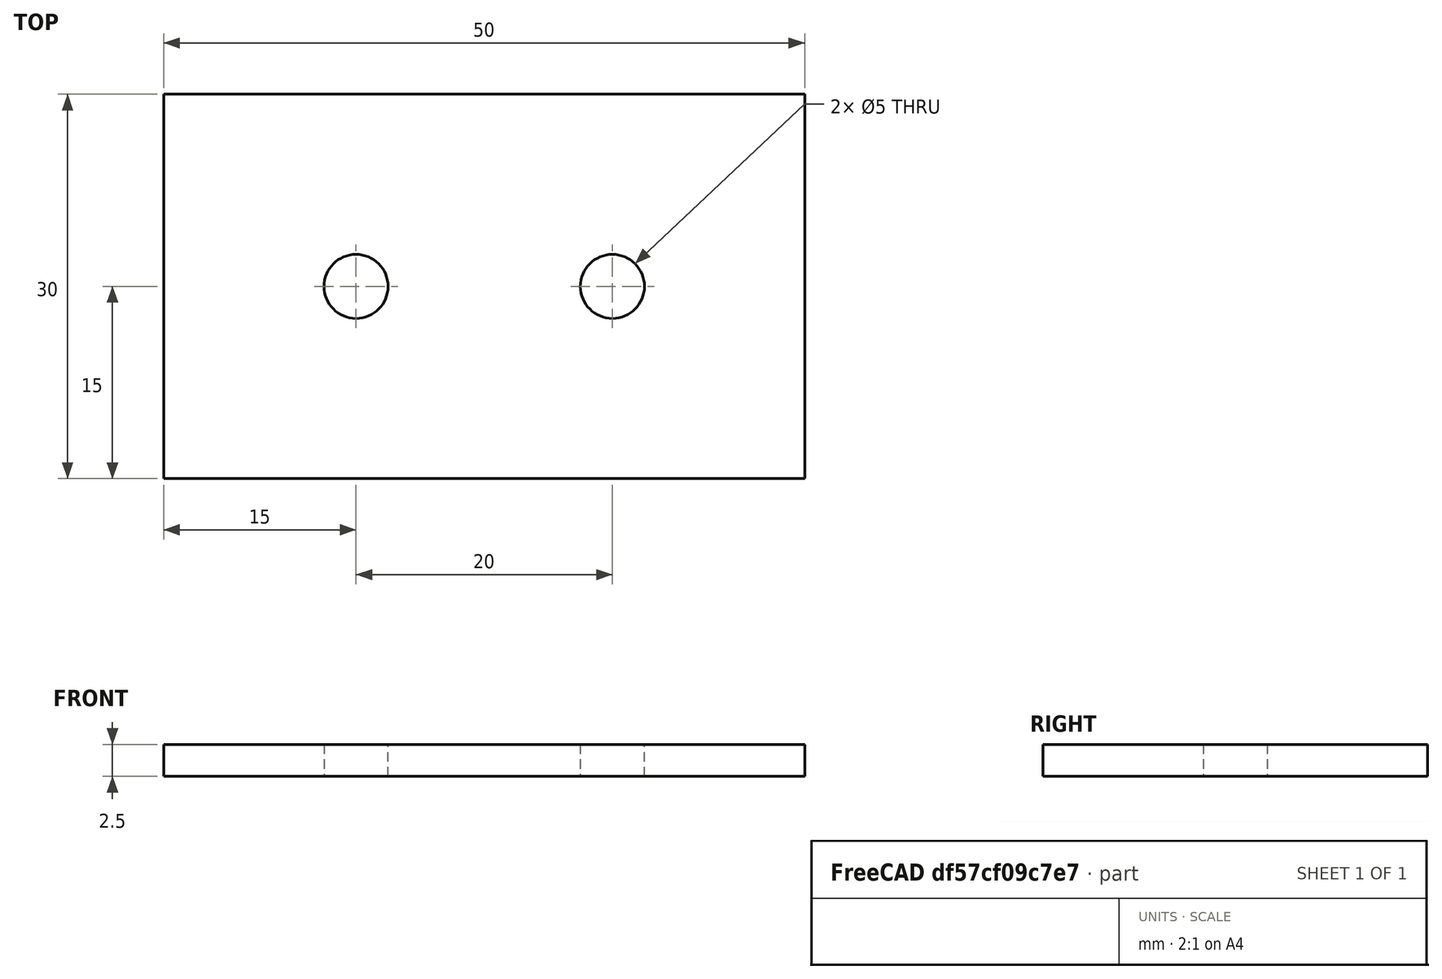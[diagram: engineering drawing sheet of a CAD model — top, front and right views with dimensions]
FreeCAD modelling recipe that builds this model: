
FCSTD DOCUMENT  (FreeCAD 0.19R24291 (Git))
Label: FiberHoldertestPlate2
License: All rights reserved
LicenseURL: http://en.wikipedia.org/wiki/All_rights_reserved
objects: Sketcher::SketchObject×1, PartDesign::Pad×1, PartDesign::Body×1
note: 4 computed .brp shape members not serialized (recipe doc carries the construction recipe); baked Part::Feature solids carry a one-line shape summary decoded from their .brp

FEATURE [Sketcher::SketchObject] Sketch
  FullyConstrained = true
  MapMode = 5
  Support = -> [XY_Plane]
  sketch-geometry (6):
    g0: LineSegment StartX=0 StartY=0 StartZ=0 EndX=50 EndY=0 EndZ=0
    g1: LineSegment StartX=50 StartY=0 StartZ=0 EndX=50 EndY=30 EndZ=0
    g2: LineSegment StartX=50 StartY=30 StartZ=0 EndX=0 EndY=30 EndZ=0
    g3: LineSegment StartX=0 StartY=30 StartZ=0 EndX=0 EndY=0 EndZ=0
    g4: Circle CenterX=15 CenterY=15 CenterZ=0 NormalX=0 NormalY=0 NormalZ=1 AngleXU=0 Radius=2.5
    g5: Circle CenterX=35 CenterY=15 CenterZ=0 NormalX=0 NormalY=0 NormalZ=1 AngleXU=0 Radius=2.5
  constraints (17):
    c: Coincident(g0,g1)
    c: Coincident(g1,g2)
    c: Coincident(g2,g3)
    c: Coincident(g3,g0)
    c: Horizontal(g0)
    c: Horizontal(g2)
    c: Vertical(g1)
    c: Vertical(g3)
    c: DistanceX(g2,g2) = 50
    c: Coincident(g0,g-1)
    c: DistanceY(g1,g1) = 30
    c: Radius(g4) = 2.5
    c: Radius(g5) = 2.5
    c: DistanceY(g4,g5) = 0
    c: DistanceX(g4,g5) = 20
    c: DistanceX(g2,g4) = 15
    c: DistanceY(g4,g2) = 15
FEATURE [PartDesign::Pad] Pad
  Direction = (1,1,1)
  Length = 2.5
  Length2 = 100
  Profile = -> Sketch
  Type = 0
FEATURE [PartDesign::Body] Body
  Group = -> [Sketch,Pad]
  Origin = -> Origin
  Tip = -> Pad
